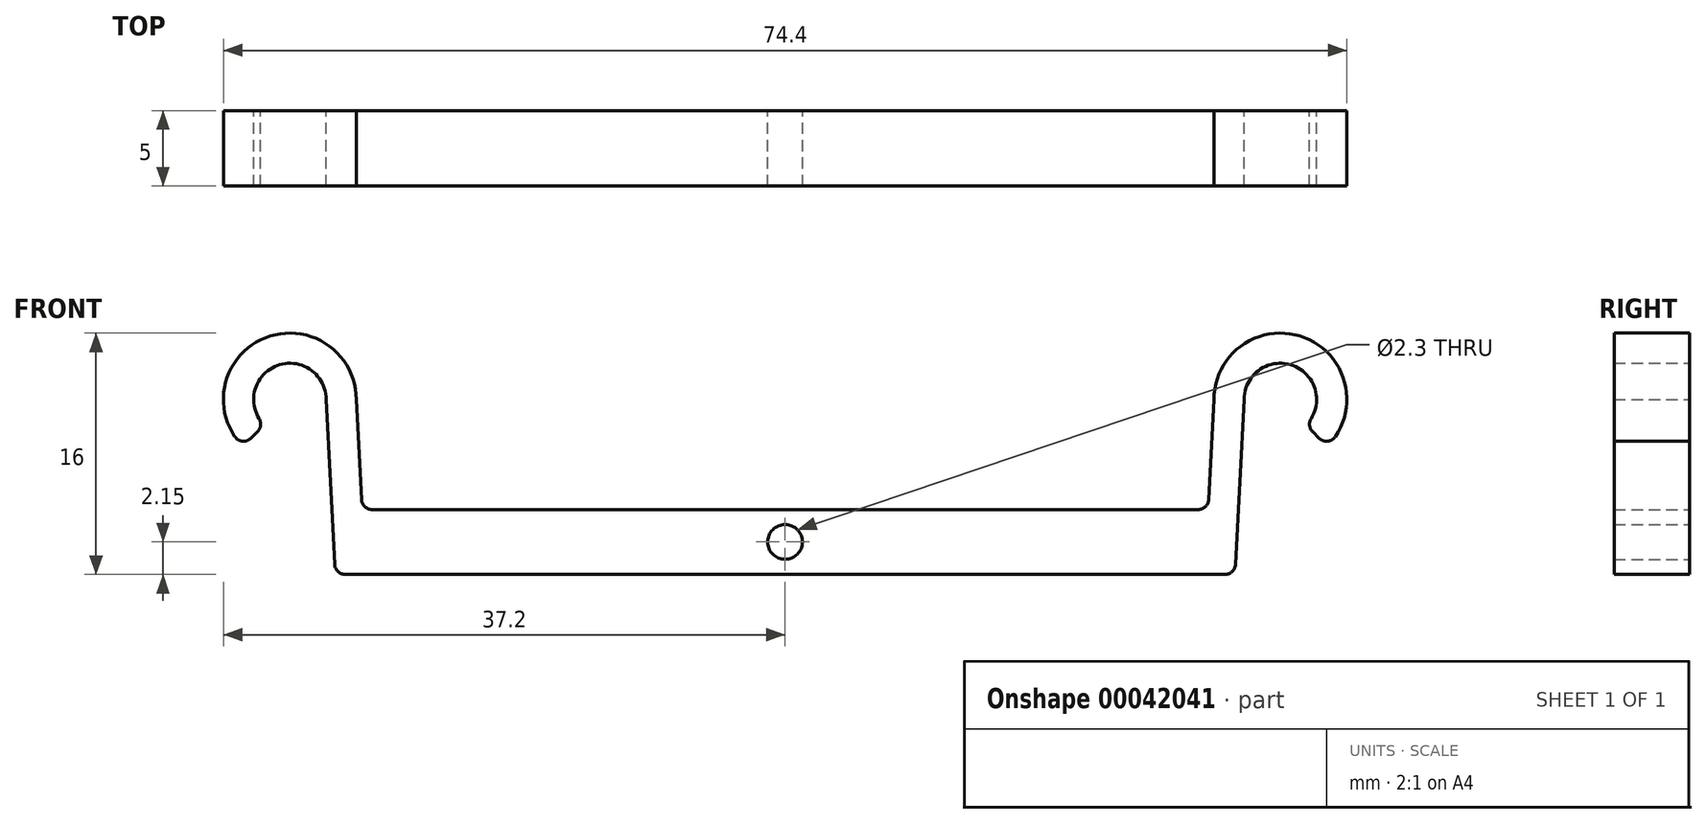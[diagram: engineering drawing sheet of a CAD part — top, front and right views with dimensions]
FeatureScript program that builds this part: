
annotation { "Feature Type Name" : "Feature", "Feature Type Description" : "" }
export const myFeature = defineFeature(function(context is Context, id is Id, definition is map)
    precondition{}
    {
        {
            var Q0;
            Q0=qCreatedBy(makeId("Front.planeOp"),FACE);
            var sketch = newSketch(context, id + "F0", { "sketchPlane" : qUnion([Q0])});
            skLineSegment(sketch, "E0", {"start": v(0, 0) * mm, "end": v(-28.02, 0) * mm});
            skLineSegment(sketch, "E1", {"start": v(-28.02, 0) * mm, "end": v(-28.4, 7.3) * mm});
            skArc(sketch, "E2", {"start": v(-28.4, 7.3) * mm, "mid": v(-34.48, 11.37) * mm, "end": v(-35.91, 4.19) * mm});
            skArc(sketch, "E3.0", {"start": v(-30.4, 7.3) * mm, "mid": v(-33.72, 9.52) * mm, "end": v(-34.5, 5.6) * mm});
            skLineSegment(sketch, "E4", {"start": v(-30.4, 7.3) * mm, "end": v(-30.4, -4.3) * mm, "construction": true});
            skLineSegment(sketch, "E5", {"start": v(-30.4, -4.3) * mm, "end": v(30.4, -4.3) * mm, "construction": true});
            skLineSegment(sketch, "E6", {"start": v(-28.4, 7.3) * mm, "end": v(-37.2, 7.3) * mm, "construction": true});
            skPoint(sketch, "E7", {"position": v(0, 0) * mm});
            skArc(sketch, "E8", {"start": v(0, -1) * mm, "mid": v(-1.15, -2.15) * mm, "end": v(0, -3.3) * mm});
            skLineSegment(sketch, "E9", {"start": v(0, 0) * mm, "end": v(0, -1) * mm});
            skPoint(sketch, "E10", {"position": v(0, -4.3) * mm});
            skPoint(sketch, "E11.orphan", {"position": v(-35.2, 7.3) * mm});
            skLineSegment(sketch, "E12", {"start": v(-35.91, 4.19) * mm, "end": v(-34.5, 5.6) * mm});
            skLineSegment(sketch, "E13", {"start": v(-30.4, 7.3) * mm, "end": v(-29.8, -4.3) * mm});
            skPoint(sketch, "E14.orphan", {"position": v(28.02, 0) * mm});
            skLineSegment(sketch, "E15", {"start": v(-29.8, -4.3) * mm, "end": v(0, -4.3) * mm});
            skLineSegment(sketch, "E16.trimOffspring", {"start": v(0, -3.3) * mm, "end": v(0, -4.3) * mm});
            skSolve(sketch);
        }
        {
            var Q0;
            Q0 = qSketchRegion(id + "F0", true);
            extrude(context, id + "F1", {"entities" : qUnion([Q0]), "depth" : 5 * mm});
        }
        {
            var Q0;
            Q0=makeQuery(id+"F1.opExtrude","SWEPT_EDGE",EDGE,{"disambiguationData":[OSD([sQuery(id+"F0.wireOp",EDGE,"E0"),sQuery(id+"F0.wireOp",EDGE,"E1")])]});
            var Q1;
            Q1=makeQuery(id+"F1.opExtrude","SWEPT_EDGE",EDGE,{"disambiguationData":[OSD([sQuery(id+"F0.wireOp",EDGE,"E13"),sQuery(id+"F0.wireOp",EDGE,"E15")])]});
            var Q2;
            Q2=makeQuery(id+"F1.opExtrude","SWEPT_EDGE",EDGE,{"disambiguationData":[OSD([sQuery(id+"F0.wireOp",EDGE,"E3.0"),sQuery(id+"F0.wireOp",EDGE,"E12")])]});
            var Q3;
            Q3=makeQuery(id+"F1.opExtrude","SWEPT_EDGE",EDGE,{"disambiguationData":[OSD([sQuery(id+"F0.wireOp",EDGE,"E2"),sQuery(id+"F0.wireOp",EDGE,"E12")])]});
            fillet(context, id + "F2", {"entities" : qUnion([Q0, Q1, Q2, Q3]), "radius" : .7 * mm, "tangentPropagation" : true, "allowEdgeOverflow" : false});
        }
        {
            var Q0;
            Q0=makeQuery(id+"F1.opExtrude","SWEPT_BODY",BODY,{"disambiguationData":[OSD([sQuery(id+"F0.wireOp",EDGE,"E0"),sQuery(id+"F0.wireOp",EDGE,"E1"),sQuery(id+"F0.wireOp",EDGE,"E2"),sQuery(id+"F0.wireOp",EDGE,"E3.0"),sQuery(id+"F0.wireOp",EDGE,"E8"),sQuery(id+"F0.wireOp",EDGE,"E9"),sQuery(id+"F0.wireOp",EDGE,"E12"),sQuery(id+"F0.wireOp",EDGE,"E13"),sQuery(id+"F0.wireOp",EDGE,"E15"),sQuery(id+"F0.wireOp",EDGE,"E16.trimOffspring")])]});
            var Q1;
            Q1=qCreatedBy(makeId("Right.planeOp"),FACE);
            mirror(context, id + "F3", {"operationType" : NewBodyOperationType.ADD, "entities" : qUnion([Q0]), "mirrorPlane" : qUnion([Q1])});
        }
    });
